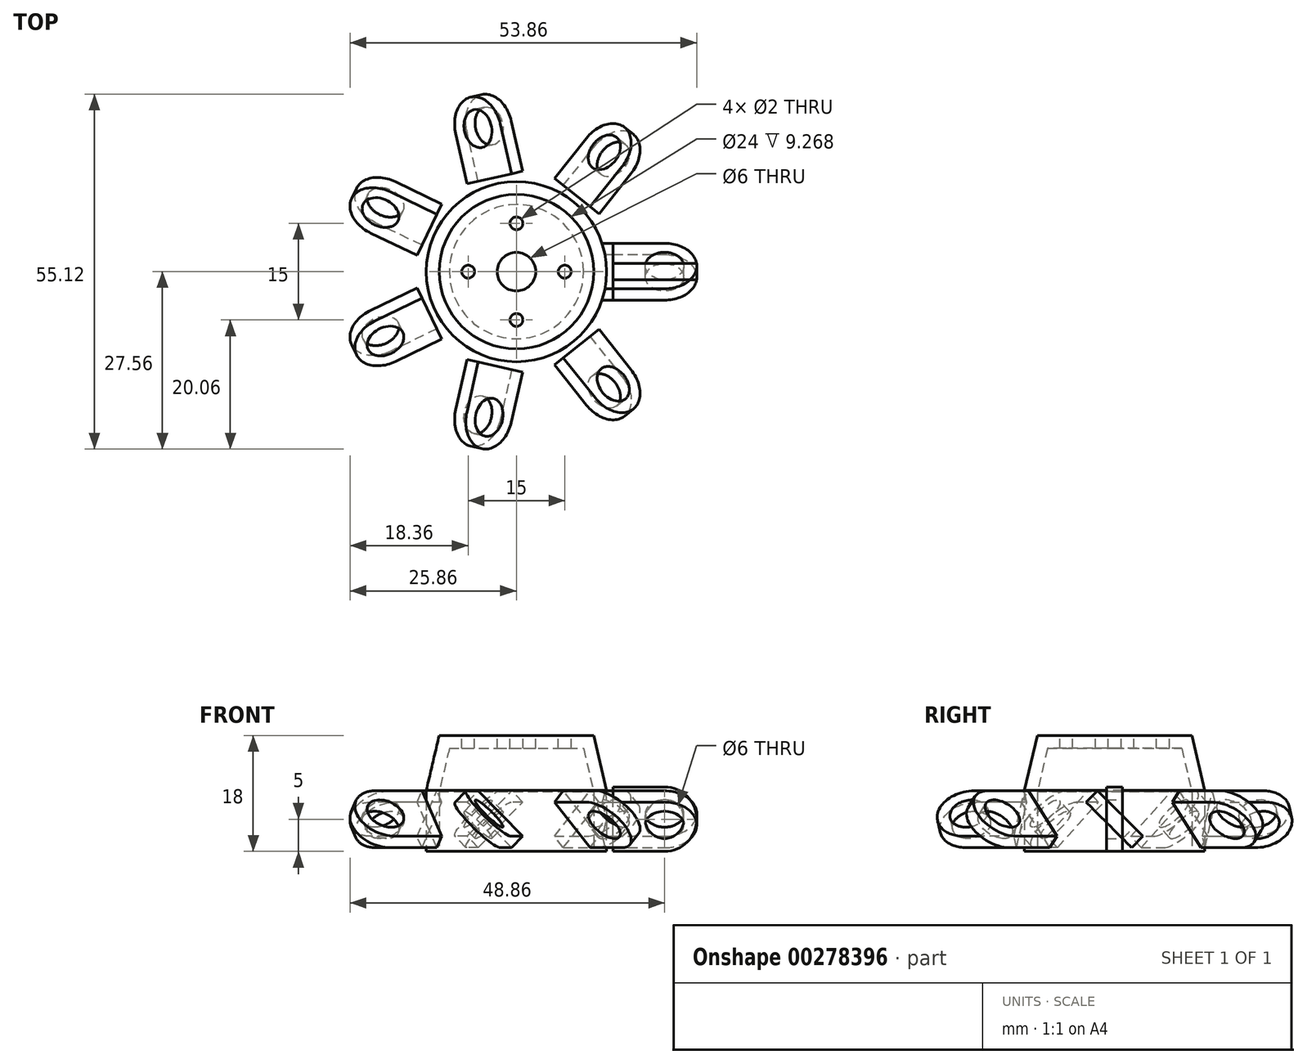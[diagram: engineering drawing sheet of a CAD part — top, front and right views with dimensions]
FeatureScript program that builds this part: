
annotation { "Feature Type Name" : "Feature", "Feature Type Description" : "" }
export const myFeature = defineFeature(function(context is Context, id is Id, definition is map)
    precondition{}
    {
        {
            var Q0;
            Q0=qCreatedBy(makeId("Front.planeOp"),FACE);
            var sketch = newSketch(context, id + "F0", { "sketchPlane" : qUnion([Q0])});
            skLineSegment(sketch, "E0.bottom", {"start": v(12, 0) * mm, "end": v(14, 0) * mm});
            skLineSegment(sketch, "E0.top", {"start": v(0, 18) * mm, "end": v(12, 18) * mm});
            skLineSegment(sketch, "E0.left", {"start": v(0, 16) * mm, "end": v(0, 18) * mm});
            skLineSegment(sketch, "E0.right", {"start": v(14, 0) * mm, "end": v(14, 9.5) * mm});
            skLineSegment(sketch, "E1", {"start": v(12, 18) * mm, "end": v(14, 9.5) * mm});
            skLineSegment(sketch, "E2", {"start": v(12, 18) * mm, "end": v(14, 18) * mm, "construction": true});
            skLineSegment(sketch, "E3", {"start": v(14, 9.5) * mm, "end": v(14, 18) * mm, "construction": true});
            skLineSegment(sketch, "E4.0", {"start": v(12, 0) * mm, "end": v(12, 9.27) * mm});
            skLineSegment(sketch, "E4.1", {"start": v(10.42, 16) * mm, "end": v(12, 9.27) * mm});
            skLineSegment(sketch, "E4.2", {"start": v(0, 16) * mm, "end": v(10.42, 16) * mm});
            skLineSegment(sketch, "E5", {"start": v(0, 0) * mm, "end": v(0, 10.56) * mm, "construction": true});
            skSolve(sketch);
        }
        {
            var Q0;
            Q0 = qSketchRegion(id + "F0", true);
            var Q1;
            Q1=sQuery(id+"F0.wireOp",EDGE,"E5");
            revolve(context, id + "F1", {"entities" : qUnion([Q0]), "axis" : qUnion([Q1]), "revolveType" : RevolveType.FULL});
        }
        {
            var Q0;
            Q0=makeQuery(id+"F1.opRevolve","SWEPT_FACE",FACE,{"disambiguationData":[OSD([sQuery(id+"F0.wireOp",EDGE,"E0.top")])]});
            var sketch = newSketch(context, id + "F2", { "sketchPlane" : qUnion([Q0])});
            skCircle(sketch, "E6", {"center": v(0, 7.5) * mm, "radius": 1 * mm});
            skCircle(sketch, "E7.1.0", {"center": v(-7.5, 0) * mm, "radius": 1 * mm});
            skCircle(sketch, "E7.2.0", {"center": v(0, -7.5) * mm, "radius": 1 * mm});
            skCircle(sketch, "E7.3.0", {"center": v(7.5, 0) * mm, "radius": 1 * mm});
            skPoint(sketch, "E7.center", {"position": v(0, 0) * mm});
            skCircle(sketch, "E8", {"center": v(0, 0) * mm, "radius": 3 * mm});
            skSolve(sketch);
        }
        {
            var Q0;
            Q0 = qSketchRegion(id + "F2", true);
            extrude(context, id + "F3", {"entities" : qUnion([Q0]), "operationType" : NewBodyOperationType.REMOVE, "endBound" : BoundingType.THROUGH_ALL, "oppositeDirection" : true, "depth" : 25 * mm});
        }
        {
            var Q0;
            Q0=qCreatedBy(makeId("Top.planeOp"),FACE);
            var sketch = newSketch(context, id + "F4", { "sketchPlane" : qUnion([Q0])});
            skLineSegment(sketch, "E9", {"start": v(0, 0) * mm, "end": v(23.1, 23.1) * mm, "construction": true});
            skSolve(sketch);
        }
        {
            var Q0;
            Q0=sQuery(id+"F0.wireOp",VERTEX,"E5.end");
            var Q1;
            Q1=sQuery(id+"F4.wireOp",VERTEX,"E9.start");
            var Q2;
            Q2=sQuery(id+"F4.wireOp",VERTEX,"E9.end");
            cPlane(context, id + "F5", {"entities" : qUnion([Q0, Q1, Q2]), "cplaneType" : CPlaneType.THREE_POINT, "offset" : 25 * mm, "width" : 150 * mm, "height" : 150 * mm});
        }
        {
            var Q0;
            Q0=qCreatedBy(makeId("Front.planeOp"),FACE);
            var sketch = newSketch(context, id + "F6", { "sketchPlane" : qUnion([Q0])});
            skLineSegment(sketch, "E10.bottom", {"start": v(14, 0) * mm, "end": v(28, 0) * mm});
            skLineSegment(sketch, "E10.top", {"start": v(14, 10) * mm, "end": v(28, 10) * mm});
            skLineSegment(sketch, "E10.left", {"start": v(14, 0) * mm, "end": v(14, 10) * mm});
            skLineSegment(sketch, "E10.right", {"start": v(28, 0) * mm, "end": v(28, 10) * mm});
            skCircle(sketch, "E11", {"center": v(23, 5) * mm, "radius": 3 * mm});
            skLineSegment(sketch, "E12", {"start": v(14, 5) * mm, "end": v(28, 5) * mm, "construction": true});
            skLineSegment(sketch, "E13", {"start": v(23, 0) * mm, "end": v(23, 10) * mm, "construction": true});
            skArc(sketch, "E14", {"start": v(23, 0) * mm, "mid": v(28, 5) * mm, "end": v(23, 10) * mm});
            skLineSegment(sketch, "E15", {"start": v(15, 0) * mm, "end": v(15, 10) * mm});
            skSolve(sketch);
        }
        {
            var Q0;
            Q0=makeQuery(id+"F6.imprint","IMPRINT",FACE,{"disambiguationData":[TD([[makeQuery(id+"F6.imprint","IMPRINT",EDGE,{"derivedFrom":sQuery(id+"F6.wireOp",EDGE,"E11")}),-1.0]])]});
            extrude(context, id + "F7", {"entities" : qUnion([Q0]), "depth" : 1.25 * mm, "hasSecondDirection" : true, "secondDirectionOppositeDirection" : true, "secondDirectionDepth" : 1.25 * mm});
        }
        {
            var Q0;
            Q0=qCreatedBy(makeId("Right.planeOp"),FACE);
            var sketch = newSketch(context, id + "F8", { "sketchPlane" : qUnion([Q0])});
            skLineSegment(sketch, "E16", {"start": v(-1.25, 5) * mm, "end": v(1.25, 5) * mm, "construction": true});
            skLineSegment(sketch, "E17", {"start": v(0, 10) * mm, "end": v(0, 0) * mm, "construction": true});
            skLineSegment(sketch, "E18", {"start": v(0, 0) * mm, "end": v(0, 5) * mm, "construction": true});
            skLineSegment(sketch, "E19", {"start": v(7.34, 12.34) * mm, "end": v(-7.64, -2.64) * mm, "construction": true});
            skSolve(sketch);
        }
        {
            var Q0;
            Q0=sQuery(id+"F6.wireOp",EDGE,"E15");
            cPoint(context, id + "F9", {"entities" : qUnion([Q0]), "parameter" : 0.5});
        }
        {
            var Q0;
            Q0=sQuery(id+"F6.wireOp",VERTEX,"E15.end");
            var Q1;
            Q1 = qCreatedBy(id + "F9" ,VERTEX);
            var Q2;
            Q2=sQuery(id+"F6.wireOp",VERTEX,"E14.center");
            cPlane(context, id + "F10", {"entities" : qUnion([Q0, Q1, Q2]), "cplaneType" : CPlaneType.THREE_POINT, "offset" : 25 * mm, "width" : 150 * mm, "height" : 150 * mm});
        }
        {
            var Q0;
            Q0=qCreatedBy(id+"F10.planeOp",FACE);
            var sketch = newSketch(context, id + "F11", { "sketchPlane" : qUnion([Q0])});
            skLineSegment(sketch, "E20", {"start": v(-13.96, 5) * mm, "end": v(-19.79, 5) * mm, "construction": true});
            skSolve(sketch);
        }
        {
            var Q0;
            Q0=makeQuery(id+"F7.opExtrude","SWEPT_BODY",BODY,{"disambiguationData":[OSD([sQuery(id+"F6.wireOp",EDGE,"E10.bottom"),sQuery(id+"F6.wireOp",EDGE,"E10.top"),sQuery(id+"F6.wireOp",EDGE,"E10.left"),sQuery(id+"F6.wireOp",EDGE,"E11"),sQuery(id+"F6.wireOp",EDGE,"E14")])]});
            var Q1;
            Q1=sQuery(id+"F11.wireOp",EDGE,"E20");
            circularPattern(context, id + "F12", {"entities" : qUnion([Q0]), "axis" : qUnion([Q1]), "angle" : 45 * degree, "instanceCount" : 2, "equalSpace" : true});
        }
        {
            var Q0;
            Q0=makeQuery(id+"F12.opPattern","COPY",FACE,{"derivedFrom":makeQuery(id+"F7.opExtrude","SWEPT_FACE",FACE,{"disambiguationData":[OSD([sQuery(id+"F6.wireOp",EDGE,"E15")])]}),"instanceName":"1"});
            var Q1;
            Q1=makeQuery(id+"F1.opRevolve","SWEPT_FACE",FACE,{"disambiguationData":[OSD([sQuery(id+"F0.wireOp",EDGE,"E0.right")])]});
            extrude(context, id + "F13", {"entities" : qUnion([Q0]), "endBound" : BoundingType.UP_TO_SURFACE, "endBoundEntityFace" : qUnion([Q1]), "depth" : 25 * mm});
        }
        {
            var Q0;
            Q0=makeQuery(id+"F12.opPattern","COPY",BODY,{"derivedFrom":makeQuery(id+"F7.opExtrude","SWEPT_BODY",BODY,{"disambiguationData":[OSD([sQuery(id+"F6.wireOp",EDGE,"E10.bottom"),sQuery(id+"F6.wireOp",EDGE,"E10.top"),sQuery(id+"F6.wireOp",EDGE,"E11"),sQuery(id+"F6.wireOp",EDGE,"E14"),sQuery(id+"F6.wireOp",EDGE,"E15")])]}),"instanceName":"1"});
            var Q1;
            Q1=sQuery(id+"F8.wireOp",EDGE,"E17");
            circularPattern(context, id + "F14", {"entities" : qUnion([Q0]), "axis" : qUnion([Q1]), "angle" : 360 * degree, "instanceCount" : 7, "equalSpace" : true});
        }
    });
